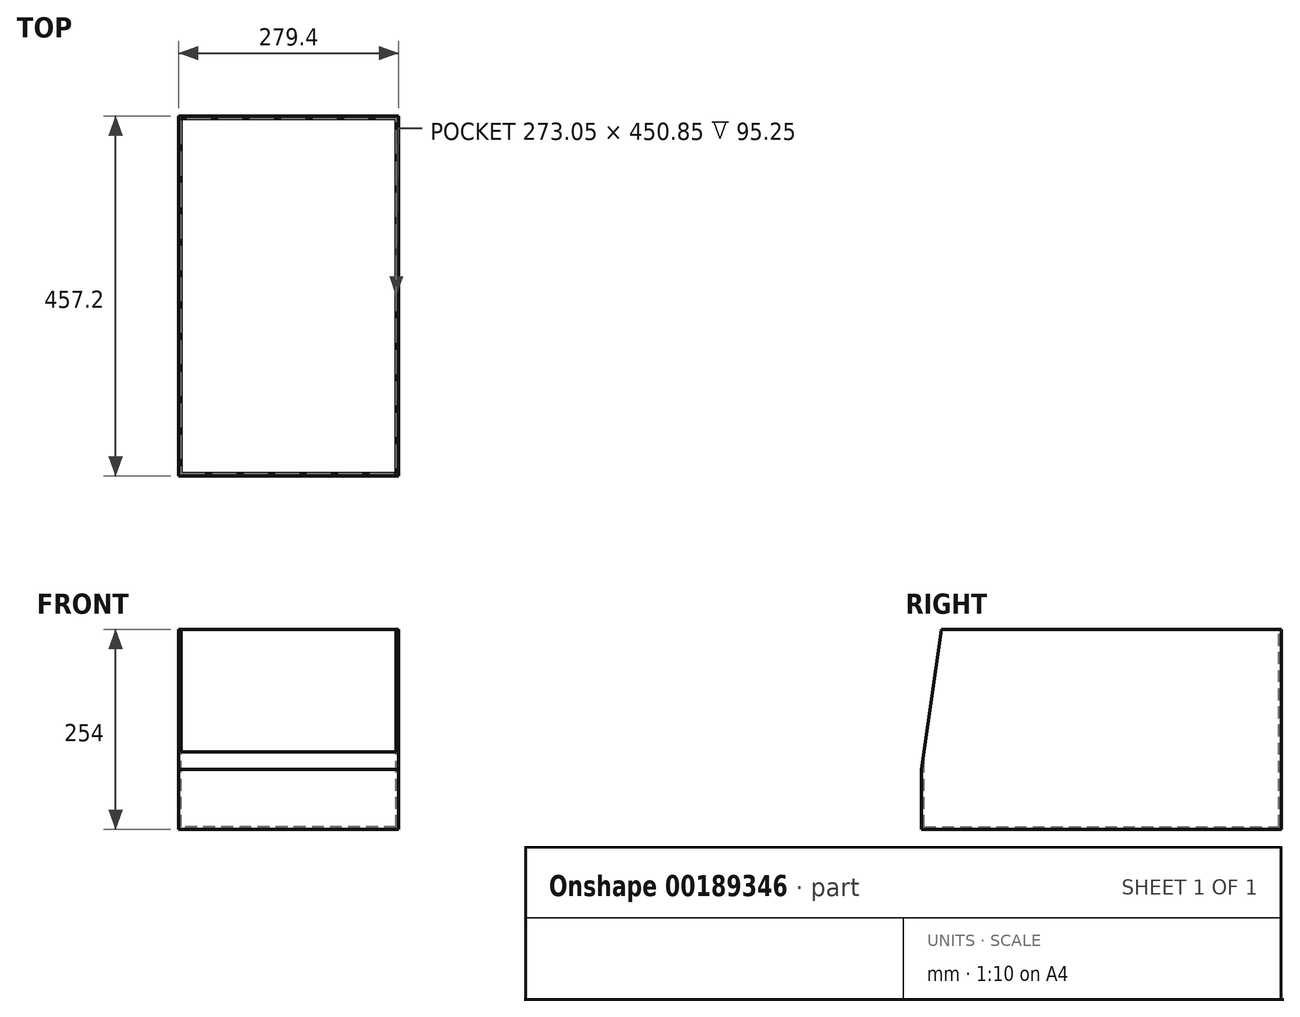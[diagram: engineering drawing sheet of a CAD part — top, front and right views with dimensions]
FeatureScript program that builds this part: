
annotation { "Feature Type Name" : "Feature", "Feature Type Description" : "" }
export const myFeature = defineFeature(function(context is Context, id is Id, definition is map)
    precondition{}
    {
        {
            var Q0;
            Q0=qCreatedBy(makeId("Right.planeOp"),FACE);
            var sketch = newSketch(context, id + "F0", { "sketchPlane" : qUnion([Q0])});
            skLineSegment(sketch, "E0.bottom", {"start": v(0, 0) * mm, "end": v(457.2, 0) * mm});
            skLineSegment(sketch, "E0.top", {"start": v(25.4, 254) * mm, "end": v(457.2, 254) * mm});
            skLineSegment(sketch, "E0.left", {"start": v(0, 0) * mm, "end": v(0, 76.2) * mm});
            skLineSegment(sketch, "E0.right", {"start": v(457.2, 0) * mm, "end": v(457.2, 254) * mm});
            skLineSegment(sketch, "E1", {"start": v(0, 76.2) * mm, "end": v(25.4, 254) * mm});
            skSolve(sketch);
        }
        {
            var Q0;
            Q0 = qSketchRegion(id + "F0", true);
            extrude(context, id + "F1", {"entities" : qUnion([Q0]), "depth" : 279.4 * mm, "symmetric" : true});
        }
        {
            var Q0;
            Q0=makeQuery(id+"F1.opExtrude","SWEPT_FACE",FACE,{"disambiguationData":[OSD([sQuery(id+"F0.wireOp",EDGE,"E0.top")])]});
            var Q1;
            Q1=makeQuery(id+"F1.opExtrude","SWEPT_FACE",FACE,{"disambiguationData":[OSD([sQuery(id+"F0.wireOp",EDGE,"E1")])]});
            shell(context, id + "F2", {"entities" : qUnion([Q0, Q1]), "thickness" : 3.17 * mm});
        }
    });
